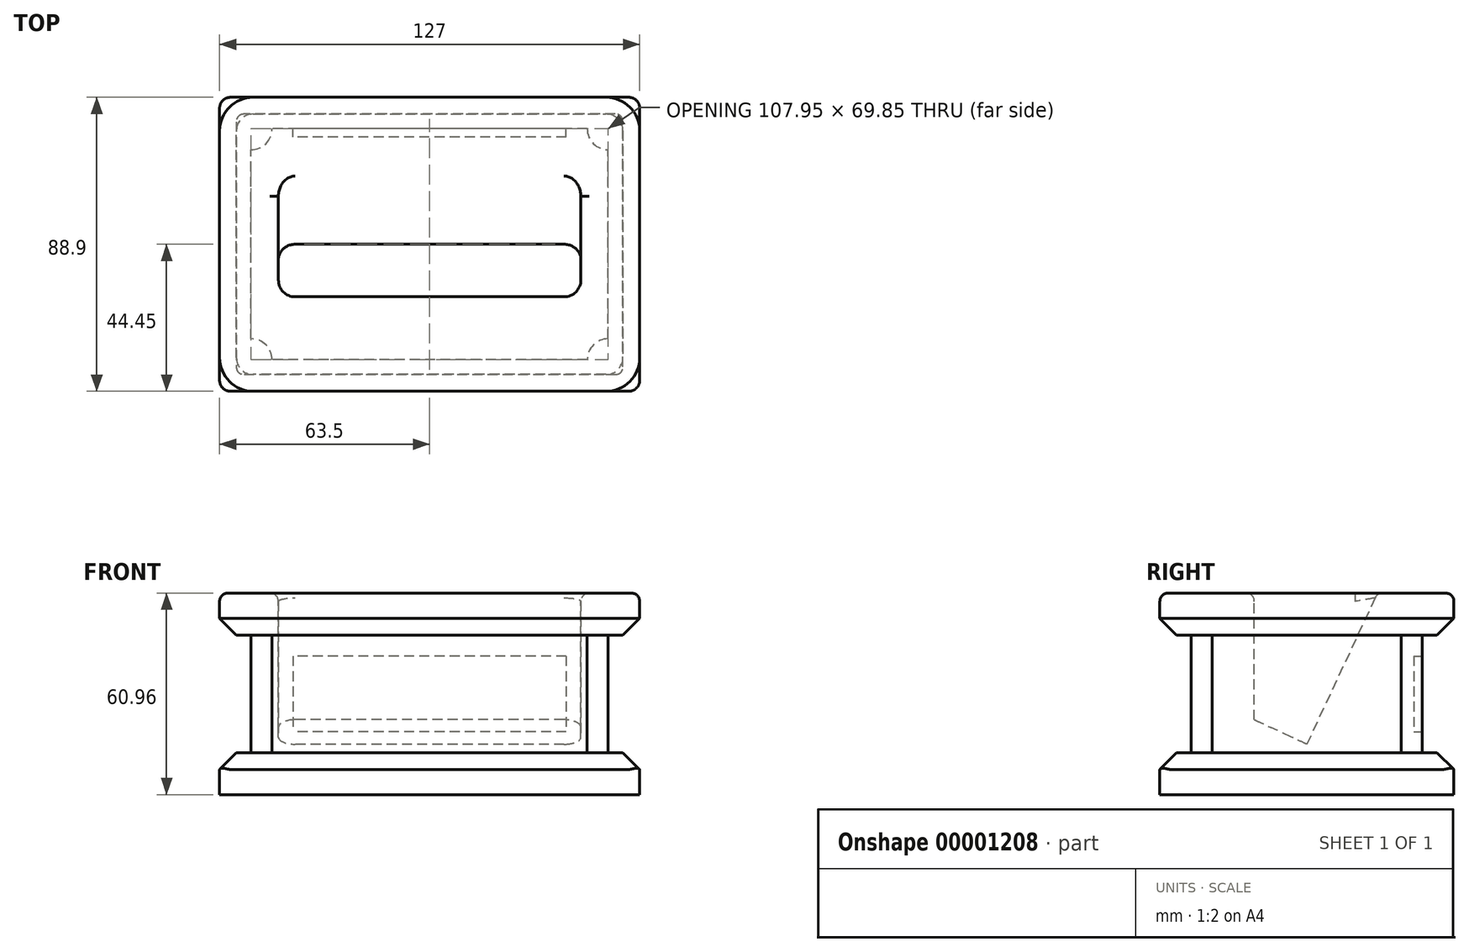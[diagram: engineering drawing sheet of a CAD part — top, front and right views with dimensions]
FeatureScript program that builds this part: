
annotation { "Feature Type Name" : "Feature", "Feature Type Description" : "" }
export const myFeature = defineFeature(function(context is Context, id is Id, definition is map)
    precondition{}
    {
        {
            var Q0;
            Q0=qCreatedBy(makeId("Top.planeOp"),FACE);
            var sketch = newSketch(context, id + "F0", { "sketchPlane" : qUnion([Q0])});
            skLineSegment(sketch, "E0.bottom", {"start": v(-63.5, 44.45) * mm, "end": v(63.5, 44.45) * mm});
            skLineSegment(sketch, "E0.top", {"start": v(-63.5, -44.45) * mm, "end": v(63.5, -44.45) * mm});
            skLineSegment(sketch, "E0.left", {"start": v(-63.5, 44.45) * mm, "end": v(-63.5, -44.45) * mm});
            skLineSegment(sketch, "E0.right", {"start": v(63.5, 44.45) * mm, "end": v(63.5, -44.45) * mm});
            skSolve(sketch);
        }
        {
            var Q0;
            Q0 = qSketchRegion(id + "F0", true);
            extrude(context, id + "F1", {"entities" : qUnion([Q0]), "depth" : 12.7 * mm, "offsetDistance" : 25.4 * mm});
        }
        {
            var Q0;
            Q0=makeQuery(id+"F1.opExtrude","CAP_FACE",FACE,{"disambiguationData":[OSD([sQuery(id+"F0.wireOp",EDGE,"E0.bottom"),sQuery(id+"F0.wireOp",EDGE,"E0.top"),sQuery(id+"F0.wireOp",EDGE,"E0.left"),sQuery(id+"F0.wireOp",EDGE,"E0.right")])],"isStart":false});
            var sketch = newSketch(context, id + "F2", { "sketchPlane" : qUnion([Q0])});
            skLineSegment(sketch, "E1.bottom", {"start": v(47.63, -34.93) * mm, "end": v(-47.62, -34.93) * mm});
            skLineSegment(sketch, "E1.top", {"start": v(47.63, 34.93) * mm, "end": v(-47.63, 34.92) * mm});
            skLineSegment(sketch, "E1.left", {"start": v(53.98, -28.58) * mm, "end": v(53.98, 28.58) * mm});
            skLineSegment(sketch, "E1.right", {"start": v(-53.97, -28.58) * mm, "end": v(-53.98, 28.57) * mm});
            skArc(sketch, "E2", {"start": v(-53.98, 28.57) * mm, "mid": v(-49.48, 30.43) * mm, "end": v(-47.63, 34.92) * mm});
            skArc(sketch, "E3", {"start": v(47.63, 34.93) * mm, "mid": v(49.48, 30.43) * mm, "end": v(53.98, 28.58) * mm});
            skArc(sketch, "E4", {"start": v(53.98, -28.58) * mm, "mid": v(49.48, -30.43) * mm, "end": v(47.63, -34.93) * mm});
            skArc(sketch, "E5", {"start": v(-47.62, -34.93) * mm, "mid": v(-49.48, -30.43) * mm, "end": v(-53.97, -28.58) * mm});
            skSolve(sketch);
        }
        {
            var Q0;
            Q0 = qSketchRegion(id + "F2", true);
            extrude(context, id + "F3", {"entities" : qUnion([Q0]), "operationType" : NewBodyOperationType.ADD, "depth" : 35.56 * mm, "offsetDistance" : 25.4 * mm});
        }
        {
            var Q0;
            Q0=makeQuery(id+"F1.opExtrude","CAP_EDGE",EDGE,{"disambiguationData":[OSD([sQuery(id+"F0.wireOp",EDGE,"E0.top")])],"isStart":false});
            var Q1;
            Q1=makeQuery(id+"F1.opExtrude","CAP_EDGE",EDGE,{"disambiguationData":[OSD([sQuery(id+"F0.wireOp",EDGE,"E0.right")])],"isStart":false});
            var Q2;
            Q2=makeQuery(id+"F1.opExtrude","CAP_EDGE",EDGE,{"disambiguationData":[OSD([sQuery(id+"F0.wireOp",EDGE,"E0.bottom")])],"isStart":false});
            var Q3;
            Q3=makeQuery(id+"F1.opExtrude","CAP_EDGE",EDGE,{"disambiguationData":[OSD([sQuery(id+"F0.wireOp",EDGE,"E0.left")])],"isStart":false});
            chamfer(context, id + "F4", {"entities" : qUnion([Q0, Q1, Q2, Q3]), "width" : 5.08 * mm, "tangentPropagation" : true});
        }
        {
            var Q0;
            Q0=makeQuery(id+"F1.opExtrude","SWEPT_EDGE",EDGE,{"disambiguationData":[OSD([sQuery(id+"F0.wireOp",EDGE,"E0.top"),sQuery(id+"F0.wireOp",EDGE,"E0.right")])]});
            var Q1;
            Q1=makeQuery(id+"F1.opExtrude","SWEPT_EDGE",EDGE,{"disambiguationData":[OSD([sQuery(id+"F0.wireOp",EDGE,"E0.bottom"),sQuery(id+"F0.wireOp",EDGE,"E0.right")])]});
            var Q2;
            Q2=makeQuery(id+"F1.opExtrude","SWEPT_EDGE",EDGE,{"disambiguationData":[OSD([sQuery(id+"F0.wireOp",EDGE,"E0.top"),sQuery(id+"F0.wireOp",EDGE,"E0.left")])]});
            var Q3;
            Q3=makeQuery(id+"F1.opExtrude","SWEPT_EDGE",EDGE,{"disambiguationData":[OSD([sQuery(id+"F0.wireOp",EDGE,"E0.bottom"),sQuery(id+"F0.wireOp",EDGE,"E0.left")])]});
            var Q4;
            Q4=makeQuery(id+"F4.opChamfer","BLEND_EDGE",EDGE,{"blendedFrom":[makeQuery(id+"F1.opExtrude","CAP_EDGE",EDGE,{"disambiguationData":[OSD([sQuery(id+"F0.wireOp",EDGE,"E0.bottom")])],"isStart":false}),makeQuery(id+"F1.opExtrude","CAP_EDGE",EDGE,{"disambiguationData":[OSD([sQuery(id+"F0.wireOp",EDGE,"E0.right")])],"isStart":false})],"blendedInto":[]});
            var Q5;
            Q5=makeQuery(id+"F4.opChamfer","BLEND_EDGE",EDGE,{"blendedFrom":[makeQuery(id+"F1.opExtrude","CAP_EDGE",EDGE,{"disambiguationData":[OSD([sQuery(id+"F0.wireOp",EDGE,"E0.bottom")])],"isStart":false}),makeQuery(id+"F1.opExtrude","CAP_EDGE",EDGE,{"disambiguationData":[OSD([sQuery(id+"F0.wireOp",EDGE,"E0.left")])],"isStart":false})],"blendedInto":[]});
            var Q6;
            Q6=makeQuery(id+"F4.opChamfer","BLEND_EDGE",EDGE,{"blendedFrom":[makeQuery(id+"F1.opExtrude","CAP_EDGE",EDGE,{"disambiguationData":[OSD([sQuery(id+"F0.wireOp",EDGE,"E0.top")])],"isStart":false}),makeQuery(id+"F1.opExtrude","CAP_EDGE",EDGE,{"disambiguationData":[OSD([sQuery(id+"F0.wireOp",EDGE,"E0.left")])],"isStart":false})],"blendedInto":[]});
            var Q7;
            Q7=makeQuery(id+"F4.opChamfer","BLEND_EDGE",EDGE,{"blendedFrom":[makeQuery(id+"F1.opExtrude","CAP_EDGE",EDGE,{"disambiguationData":[OSD([sQuery(id+"F0.wireOp",EDGE,"E0.top")])],"isStart":false}),makeQuery(id+"F1.opExtrude","CAP_EDGE",EDGE,{"disambiguationData":[OSD([sQuery(id+"F0.wireOp",EDGE,"E0.right")])],"isStart":false})],"blendedInto":[]});
            fillet(context, id + "F5", {"entities" : qUnion([Q0, Q1, Q2, Q3, Q4, Q5, Q6, Q7]), "tangentPropagation" : true, "radius" : 3.3 * mm, "defaultsChanged" : false, "vertexSettings" : [], "allowEdgeOverflow" : false});
        }
        {
            var Q0;
            Q0=makeQuery(id+"F3.opExtrude","CAP_FACE",FACE,{"disambiguationData":[OSD([sQuery(id+"F2.wireOp",EDGE,"E1.bottom"),sQuery(id+"F2.wireOp",EDGE,"E1.top"),sQuery(id+"F2.wireOp",EDGE,"E1.left"),sQuery(id+"F2.wireOp",EDGE,"E1.right"),sQuery(id+"F2.wireOp",EDGE,"E2"),sQuery(id+"F2.wireOp",EDGE,"E3"),sQuery(id+"F2.wireOp",EDGE,"E4"),sQuery(id+"F2.wireOp",EDGE,"E5")])],"isStart":false});
            var sketch = newSketch(context, id + "F6", { "sketchPlane" : qUnion([Q0])});
            skLineSegment(sketch, "E6.bottom", {"start": v(-63.5, -44.45) * mm, "end": v(63.5, -44.45) * mm});
            skLineSegment(sketch, "E6.top", {"start": v(-63.5, 44.45) * mm, "end": v(63.5, 44.45) * mm});
            skLineSegment(sketch, "E6.left", {"start": v(-63.5, -44.45) * mm, "end": v(-63.5, 44.45) * mm});
            skLineSegment(sketch, "E6.right", {"start": v(63.5, -44.45) * mm, "end": v(63.5, 44.45) * mm});
            skSolve(sketch);
        }
        {
            var Q0;
            Q0 = qSketchRegion(id + "F6", true);
            extrude(context, id + "F7", {"entities" : qUnion([Q0]), "operationType" : NewBodyOperationType.ADD, "depth" : 12.7 * mm, "offsetDistance" : 25.4 * mm});
        }
        {
            var Q0;
            Q0=makeQuery(id+"F7.opExtrude","SWEPT_EDGE",EDGE,{"disambiguationData":[OSD([sQuery(id+"F6.wireOp",EDGE,"E6.bottom"),sQuery(id+"F6.wireOp",EDGE,"E6.right")])]});
            var Q1;
            Q1=makeQuery(id+"F7.opExtrude","SWEPT_EDGE",EDGE,{"disambiguationData":[OSD([sQuery(id+"F6.wireOp",EDGE,"E6.bottom"),sQuery(id+"F6.wireOp",EDGE,"E6.left")])]});
            var Q2;
            Q2=makeQuery(id+"F7.opExtrude","SWEPT_EDGE",EDGE,{"disambiguationData":[OSD([sQuery(id+"F6.wireOp",EDGE,"E6.top"),sQuery(id+"F6.wireOp",EDGE,"E6.left")])]});
            var Q3;
            Q3=makeQuery(id+"F7.opExtrude","SWEPT_EDGE",EDGE,{"disambiguationData":[OSD([sQuery(id+"F6.wireOp",EDGE,"E6.top"),sQuery(id+"F6.wireOp",EDGE,"E6.right")])]});
            fillet(context, id + "F8", {"entities" : qUnion([Q0, Q1, Q2, Q3]), "tangentPropagation" : true, "radius" : 10.16 * mm, "defaultsChanged" : true, "vertexSettings" : [], "allowEdgeOverflow" : false});
        }
        {
            var Q0;
            Q0=makeQuery(id+"F7.opExtrude","CAP_EDGE",EDGE,{"disambiguationData":[OSD([sQuery(id+"F6.wireOp",EDGE,"E6.top")])],"isStart":true});
            chamfer(context, id + "F9", {"entities" : qUnion([Q0]), "width" : 5.08 * mm, "tangentPropagation" : true});
        }
        {
            var Q0;
            Q0=makeQuery(id+"F3.opExtrude","SWEPT_FACE",FACE,{"disambiguationData":[OSD([sQuery(id+"F2.wireOp",EDGE,"E1.top")])]});
            var sketch = newSketch(context, id + "F10", { "sketchPlane" : qUnion([Q0])});
            skLineSegment(sketch, "E7.bottom", {"start": v(-41.28, 41.9) * mm, "end": v(41.27, 41.91) * mm});
            skLineSegment(sketch, "E7.top", {"start": v(-41.28, 19.05) * mm, "end": v(41.27, 19.05) * mm});
            skLineSegment(sketch, "E7.left", {"start": v(-41.28, 41.9) * mm, "end": v(-41.28, 19.05) * mm});
            skLineSegment(sketch, "E7.right", {"start": v(41.27, 41.91) * mm, "end": v(41.27, 19.05) * mm});
            skSolve(sketch);
        }
        {
            var Q0;
            Q0 = qSketchRegion(id + "F10", true);
            extrude(context, id + "F11", {"entities" : qUnion([Q0]), "operationType" : NewBodyOperationType.REMOVE, "oppositeDirection" : true, "depth" : 2.54 * mm, "offsetDistance" : 25.4 * mm});
        }
        {
            var Q0;
            Q0=qCreatedBy(makeId("Right.planeOp"),FACE);
            var sketch = newSketch(context, id + "F12", { "sketchPlane" : qUnion([Q0])});
            skLineSegment(sketch, "E8", {"start": v(21.91, 62.23) * mm, "end": v(0, 15.24) * mm});
            skLineSegment(sketch, "E9", {"start": v(0, 15.24) * mm, "end": v(-15.88, 22.64) * mm});
            skLineSegment(sketch, "E10", {"start": v(-15.88, 22.64) * mm, "end": v(-15.88, 62.23) * mm});
            skLineSegment(sketch, "E11", {"start": v(-15.88, 62.23) * mm, "end": v(21.91, 62.23) * mm});
            skSolve(sketch);
        }
        {
            var Q0;
            Q0 = qSketchRegion(id + "F12", true);
            extrude(context, id + "F13", {"entities" : qUnion([Q0]), "operationType" : NewBodyOperationType.REMOVE, "depth" : 91.44 * mm, "offsetDistance" : 25.4 * mm, "symmetric" : true});
        }
        {
            var Q0;
            Q0=makeQuery(id+"F13.boolean.opBoolean","COPY",EDGE,{"derivedFrom":makeQuery(id+"F13.opExtrude","CAP_EDGE",EDGE,{"disambiguationData":[OSD([sQuery(id+"F12.wireOp",EDGE,"E8")])],"isStart":true})});
            var Q1;
            Q1=makeQuery(id+"F13.boolean.opBoolean","COPY",EDGE,{"derivedFrom":makeQuery(id+"F13.opExtrude","CAP_EDGE",EDGE,{"disambiguationData":[OSD([sQuery(id+"F12.wireOp",EDGE,"E10")])],"isStart":true})});
            var Q2;
            Q2=makeQuery(id+"F13.boolean.opBoolean","COPY",EDGE,{"derivedFrom":makeQuery(id+"F13.opExtrude","CAP_EDGE",EDGE,{"disambiguationData":[OSD([sQuery(id+"F12.wireOp",EDGE,"E10")])],"isStart":false})});
            var Q3;
            Q3=makeQuery(id+"F13.boolean.opBoolean","COPY",EDGE,{"derivedFrom":makeQuery(id+"F13.opExtrude","CAP_EDGE",EDGE,{"disambiguationData":[OSD([sQuery(id+"F12.wireOp",EDGE,"E8")])],"isStart":false})});
            fillet(context, id + "F14", {"entities" : qUnion([Q0, Q1, Q2, Q3]), "tangentPropagation" : true, "radius" : 5.08 * mm, "defaultsChanged" : false, "vertexSettings" : [], "allowEdgeOverflow" : false});
        }
        {
            var Q0;
            Q0=makeQuery(id+"F13.boolean.opBoolean","INTERSECT",EDGE,{"derivedFrom":[makeQuery(id+"F7.opExtrude","CAP_FACE",FACE,{"disambiguationData":[OSD([sQuery(id+"F6.wireOp",EDGE,"E6.bottom"),sQuery(id+"F6.wireOp",EDGE,"E6.top"),sQuery(id+"F6.wireOp",EDGE,"E6.left"),sQuery(id+"F6.wireOp",EDGE,"E6.right")])],"isStart":false}),makeQuery(id+"F13.opExtrude","SWEPT_FACE",FACE,{"disambiguationData":[OSD([sQuery(id+"F12.wireOp",EDGE,"E8")])]})]});
            var Q1;
            Q1=makeQuery(id+"F7.opExtrude","CAP_EDGE",EDGE,{"disambiguationData":[OSD([sQuery(id+"F6.wireOp",EDGE,"E6.left")])],"isStart":false});
            fillet(context, id + "F15", {"entities" : qUnion([Q0, Q1]), "tangentPropagation" : true, "radius" : 2.54 * mm, "defaultsChanged" : true, "vertexSettings" : [], "allowEdgeOverflow" : false});
        }
    });
